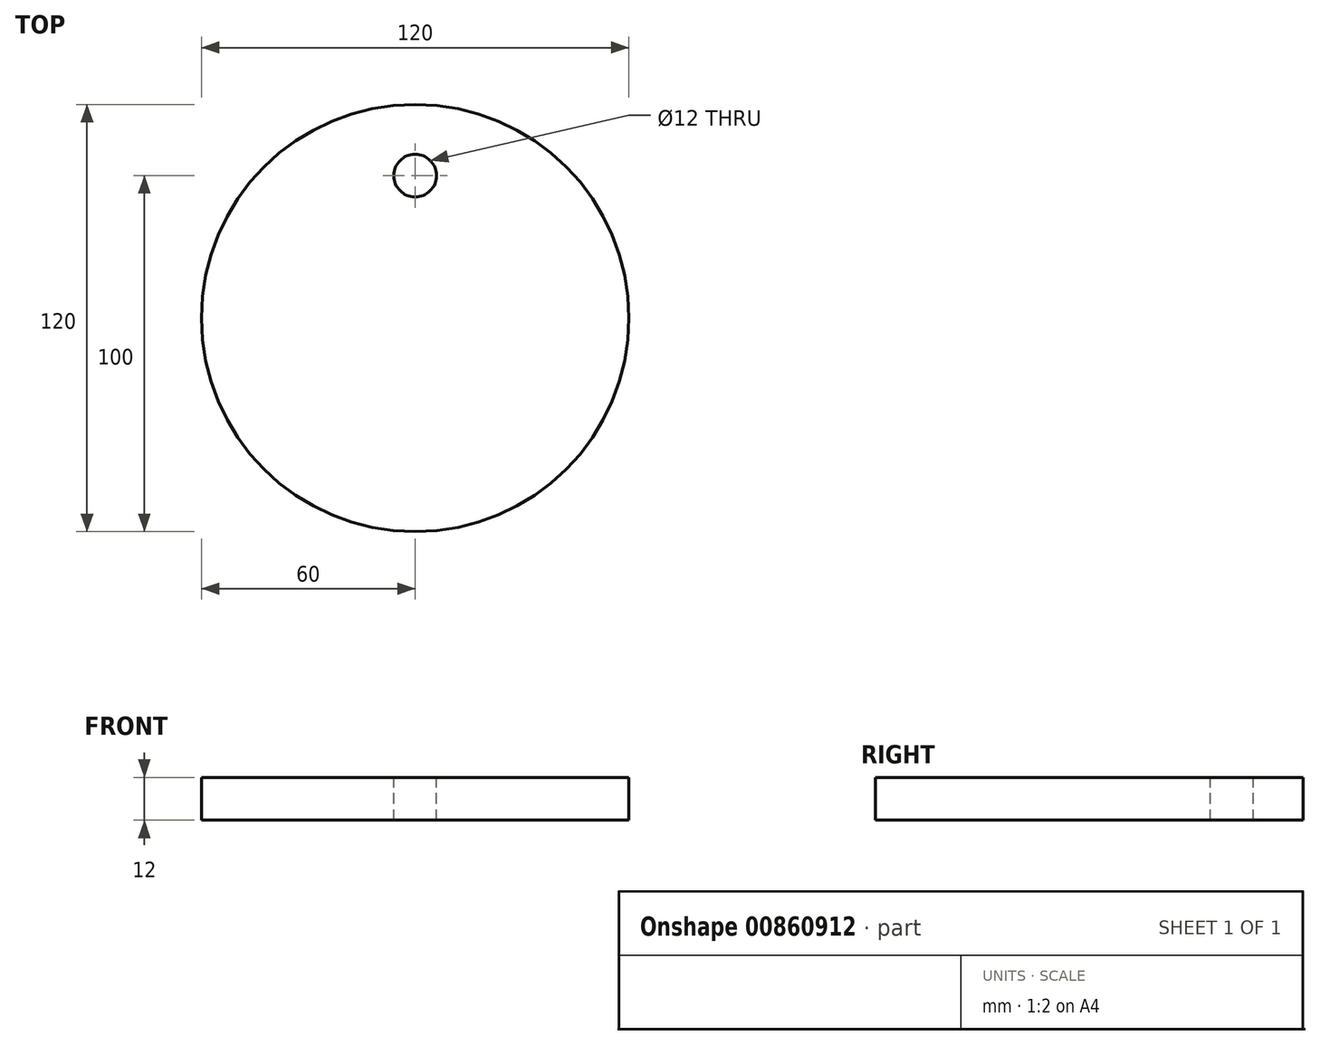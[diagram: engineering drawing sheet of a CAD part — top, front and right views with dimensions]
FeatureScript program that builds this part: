
annotation { "Feature Type Name" : "Feature", "Feature Type Description" : "" }
export const myFeature = defineFeature(function(context is Context, id is Id, definition is map)
    precondition{}
    {
        {
            var Q0;
            Q0=qCreatedBy(makeId("Top.planeOp"),FACE);
            var sketch = newSketch(context, id + "F0", { "sketchPlane" : qUnion([Q0])});
            skCircle(sketch, "E0", {"center": v(0, 0) * mm, "radius": 60 * mm});
            skSolve(sketch);
        }
        {
            var Q0;
            Q0 = qSketchRegion(id + "F0", true);
            extrude(context, id + "F1", {"entities" : qUnion([Q0]), "depth" : 12 * mm, "offsetDistance" : 25 * mm});
        }
        {
            var Q0;
            Q0=makeQuery(id+"F1.opExtrude","CAP_FACE",FACE,{"disambiguationData":[OSD([sQuery(id+"F0.wireOp",EDGE,"E0")])],"isStart":false});
            var sketch = newSketch(context, id + "F2", { "sketchPlane" : qUnion([Q0])});
            skCircle(sketch, "E1", {"center": v(0, 0) * mm, "radius": 40 * mm, "construction": true});
            skCircle(sketch, "E2", {"center": v(0, 40) * mm, "radius": 6 * mm});
            skSolve(sketch);
        }
        {
            var Q0;
            Q0=makeQuery(id+"F2.imprint","IMPRINT",FACE,{"disambiguationData":[TD([[makeQuery(id+"F2.imprint","IMPRINT",EDGE,{"derivedFrom":sQuery(id+"F2.wireOp",EDGE,"E2")}),1.0]])]});
            var Q1;
            Q1=sQuery(id+"F2.wireOp",EDGE,"E2");
            extrude(context, id + "F3", {"entities" : qUnion([Q0]), "operationType" : NewBodyOperationType.REMOVE, "surfaceEntities" : qUnion([Q1]), "endBound" : BoundingType.THROUGH_ALL, "oppositeDirection" : true, "depth" : 25 * mm, "offsetDistance" : 25 * mm});
        }
    });
